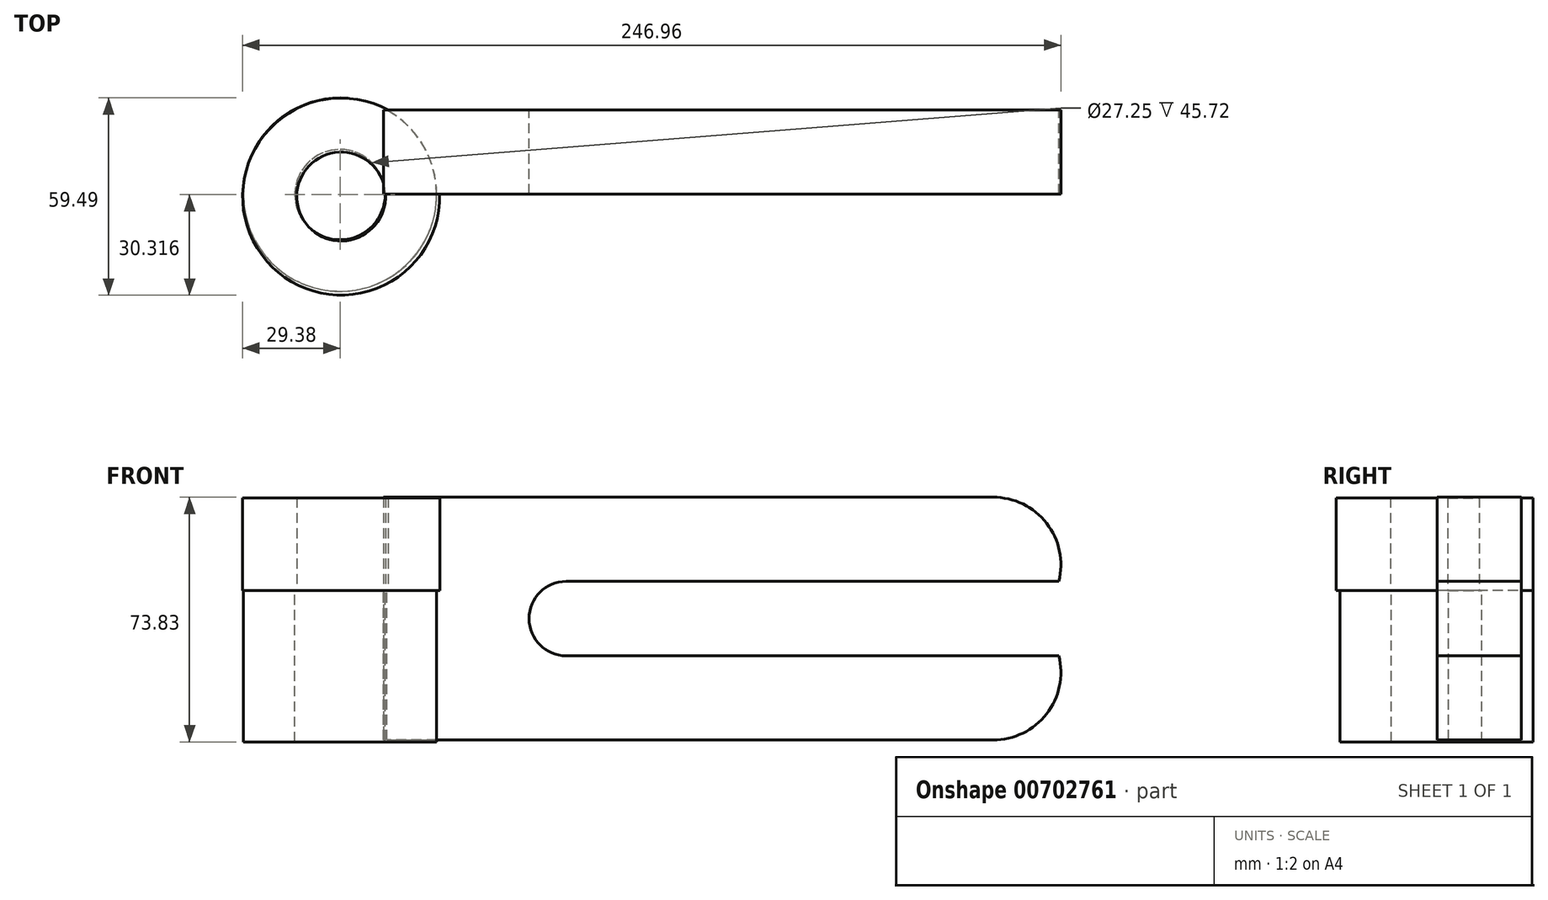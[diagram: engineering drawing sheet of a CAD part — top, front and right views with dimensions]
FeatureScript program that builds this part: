
annotation { "Feature Type Name" : "Feature", "Feature Type Description" : "" }
export const myFeature = defineFeature(function(context is Context, id is Id, definition is map)
    precondition{}
    {
        {
            var Q0;
            Q0=qCreatedBy(makeId("Front.planeOp"),FACE);
            var sketch = newSketch(context, id + "F0", { "sketchPlane" : qUnion([Q0])});
            skLineSegment(sketch, "E0", {"start": v(-57.87, 28.11) * mm, "end": v(126.13, 28.11) * mm});
            skLineSegment(sketch, "E1", {"start": v(145.95, 2.71) * mm, "end": v(-2.73, 2.71) * mm});
            skLineSegment(sketch, "E2.MirrorCS", {"start": v(145.95, -19.74) * mm, "end": v(-2.73, -19.74) * mm});
            skLineSegment(sketch, "E3.MirrorCS", {"start": v(-57.87, -45.14) * mm, "end": v(126.13, -45.14) * mm});
            skPoint(sketch, "E4.start.orphan", {"position": v(-38.32, -8.51) * mm});
            skPoint(sketch, "E5.end.orphan", {"position": v(-2.73, -8.51) * mm});
            skArc(sketch, "E6", {"start": v(-2.73, 2.71) * mm, "mid": v(-13.96, -8.51) * mm, "end": v(-2.73, -19.74) * mm});
            skArc(sketch, "E7", {"start": v(145.95, 2.71) * mm, "mid": v(142.24, 20.25) * mm, "end": v(126.13, 28.11) * mm});
            skArc(sketch, "E8", {"start": v(126.13, -45.14) * mm, "mid": v(142.24, -37.28) * mm, "end": v(145.95, -19.74) * mm});
            skLineSegment(sketch, "E9", {"start": v(-57.87, 28.11) * mm, "end": v(-57.87, -45.14) * mm});
            skSolve(sketch);
        }
        {
            var Q0;
            Q0 = qSketchRegion(id + "F0", true);
            extrude(context, id + "F1", {"entities" : qUnion([Q0]), "depth" : 25.4 * mm, "offsetDistance" : 25.4 * mm});
        }
        {
            var Q0;
            Q0=qCreatedBy(makeId("Top.planeOp"),FACE);
            var sketch = newSketch(context, id + "F2", { "sketchPlane" : qUnion([Q0])});
            skCircle(sketch, "E10", {"center": v(-70.67, -26.13) * mm, "radius": 29.73 * mm});
            skCircle(sketch, "E11", {"center": v(-70.67, -26.13) * mm, "radius": 13.4 * mm});
            skSolve(sketch);
        }
        {
            var Q0;
            Q0 = qSketchRegion(id + "F2", true);
            extrude(context, id + "F3", {"entities" : qUnion([Q0]), "operationType" : NewBodyOperationType.ADD, "depth" : 27.94 * mm, "offsetDistance" : 25.4 * mm});
        }
        {
            var Q0;
            Q0=qCreatedBy(makeId("Top.planeOp"),FACE);
            var sketch = newSketch(context, id + "F4", { "sketchPlane" : qUnion([Q0])});
            skCircle(sketch, "E12", {"center": v(-71.02, -25.54) * mm, "radius": 13.62 * mm});
            skCircle(sketch, "E13", {"center": v(-71.02, -25.54) * mm, "radius": 29.17 * mm});
            skSolve(sketch);
        }
        {
            var Q0;
            Q0 = qSketchRegion(id + "F4", true);
            extrude(context, id + "F5", {"entities" : qUnion([Q0]), "operationType" : NewBodyOperationType.ADD, "oppositeDirection" : true, "depth" : 45.72 * mm, "offsetDistance" : 25.4 * mm});
        }
    });
